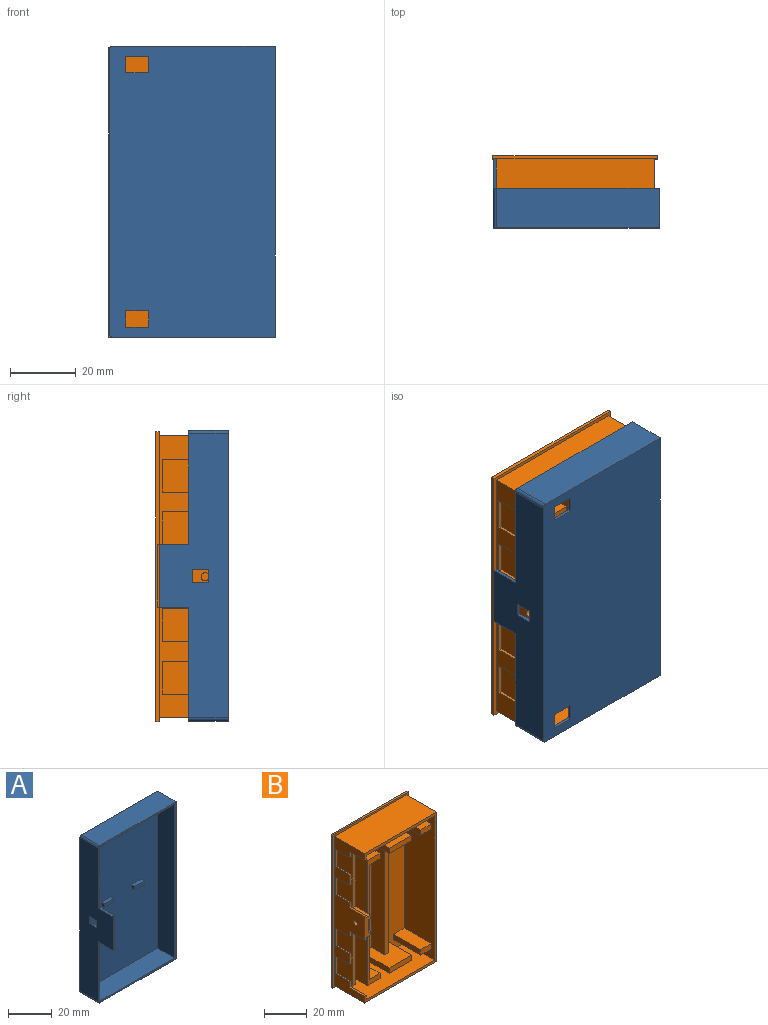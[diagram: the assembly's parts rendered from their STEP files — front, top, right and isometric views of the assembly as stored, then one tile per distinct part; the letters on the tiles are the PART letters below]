
ASSEMBLY  parts=2 mates=1
PART A: 38 faces, bbox 50.5x21.5x88.5 mm
  f0: plane 86.5x21.5mm, normal (-1,0,0), area 1198.5mm2, adj f2,f3,f16,f20,f21,f22,f23,f34
  f1: plane 86.5x20.5mm, normal (1,0,0), area 1112mm2, adj f15,f17,f19,f20,f21,f22,f23,f34
  f2: cylinder r=1mm len=12mm, axis (0,1,0), area 18.8mm2, adj f0,f14,f16,f20
  f3: cylinder r=1mm len=12mm, axis (0,1,0), area 18.8mm2, adj f0,f4,f16,f20
  f4: plane 49.5x12mm, normal (0,0,-1), area 594mm2, adj f3,f5,f16,f20
  f5: plane 88.5x12mm, normal (1,0,0), area 1062mm2, adj f4,f14,f16,f20
  f6: plane 5x1mm, normal (1,0,0), area 5mm2, adj f7,f12,f15,f16
  f7: plane 7x1mm, normal (0,0,-1), area 7mm2, adj f6,f8,f15,f16
  f8: plane 5x1mm, normal (-1,0,0), area 5mm2, adj f7,f12,f15,f16
  f9: plane 7x1mm, normal (0,0,1), area 7mm2, adj f10,f13,f15,f16
  f10: plane 5x1mm, normal (1,0,0), area 5mm2, adj f9,f11,f15,f16
  f11: plane 7x1mm, normal (0,0,-1), area 7mm2, adj f10,f13,f15,f16
  f12: plane 7x1mm, normal (0,0,1), area 7mm2, adj f6,f8,f15,f16
  f13: plane 5x1mm, normal (-1,0,0), area 5mm2, adj f9,f11,f15,f16
  f14: plane 49.5x12mm, normal (0,0,1), area 594mm2, adj f2,f5,f16,f20
  f15: plane 86.5x48.5mm, normal (0,-1,0), area 4101.2mm2, adj f1,f6,f7,f8,f9,f10,f11,f12
  f16: plane 88.5x50.5mm, normal (0,1,0), area 4398.8mm2, adj f0,f2,f3,f4,f5,f6,f7,f8
  f17: plane 48.5x11mm, normal (0,0,-1), area 533.5mm2, adj f1,f15,f18,f20
  f18: plane 86.5x11mm, normal (-1,0,0), area 951.5mm2, adj f15,f17,f19,f20
  f19: plane 48.5x11mm, normal (0,0,1), area 533.5mm2, adj f1,f15,f18,f20
  f20: plane 88.5x50.5mm, normal (0,-1,0), area 254.6mm2, adj f0,f1,f2,f3,f4,f5,f14,f17
  f21: plane 9.5x1mm, normal (0,0,1), area 9.5mm2, adj f0,f1,f20,f23
  f22: plane 9.5x1mm, normal (0,0,-1), area 9.5mm2, adj f0,f1,f20,f23
  f23: plane 19x1mm, normal (0,-1,0), area 19mm2, adj f0,f1,f21,f22
  f24: plane 6x2mm, normal (0,0,1), area 12mm2, adj f15,f25,f27,f28
  f25: plane 2x2mm, normal (-1,0,0), area 4mm2, adj f15,f24,f26,f28
  f26: plane 6x2mm, normal (0,0,-1), area 12mm2, adj f15,f25,f27,f28
  f27: plane 2x2mm, normal (1,0,0), area 4mm2, adj f15,f24,f26,f28
  f28: plane 6x2mm, normal (0,-1,0), area 12mm2, adj f24,f25,f26,f27
  f29: plane 6x2mm, normal (0,0,1), area 12mm2, adj f15,f30,f32,f33
  f30: plane 2x2mm, normal (-1,0,0), area 4mm2, adj f15,f29,f31,f33
  f31: plane 6x2mm, normal (0,0,-1), area 12mm2, adj f15,f30,f32,f33
  f32: plane 2x2mm, normal (1,0,0), area 4mm2, adj f15,f29,f31,f33
  f33: plane 6x2mm, normal (0,-1,0), area 12mm2, adj f29,f30,f31,f32
  f34: plane 5x1mm, normal (0,0,-1), area 5mm2, adj f0,f1,f35,f37
  f35: plane 4x1mm, normal (0,-1,0), area 4mm2, adj f0,f1,f34,f36
  f36: plane 5x1mm, normal (0,0,1), area 5mm2, adj f0,f1,f35,f37
  f37: plane 4x1mm, normal (0,1,0), area 4mm2, adj f0,f1,f34,f36
PART B: 103 faces, bbox 50.2x21x88.2 mm
  f0: plane 88.2x50.2mm, normal (0,-1,0), area 299.6mm2, adj f11,f12,f13,f14,f22,f23,f24,f25
  f1: plane 15x1mm, normal (0,-1,0), area 15mm2, adj f57,f94,f95,f96
  f2: plane 83x45.5mm, normal (0,-1,0), area 3113.8mm2, adj f8,f9,f10,f17,f18,f19,f20,f27
  f3: plane 15x1mm, normal (0,-1,0), area 15mm2, adj f61,f98,f99,f100
  f4: plane 15x1mm, normal (0,-1,0), area 15mm2, adj f59,f82,f83,f84
  f5: plane 7.5x7mm, normal (-1,0,0), area 52.5mm2, adj f35,f65,f67,f75
  f6: plane 30.25x8mm, normal (-1,0,0), area 242mm2, adj f27,f35,f68,f88
  f7: plane 15x1mm, normal (0,-1,0), area 15mm2, adj f55,f85,f86,f87
  f8: plane 18x14.91mm, normal (0,0,-1), area 244.1mm2, adj f2,f45,f46,f47,f52,f53,f54
  f9: plane 18x14.91mm, normal (0,0,1), area 244.1mm2, adj f2,f49,f50,f51,f52,f53,f54
  f10: plane 83x20mm, normal (-1,0,0), area 1552mm2, adj f2,f18,f19,f26,f36,f38,f39,f40
  f11: plane 50.2x1mm, normal (0,0,1), area 50.2mm2, adj f0,f12,f14,f15
  f12: plane 88.2x1mm, normal (-1,0,0), area 88.2mm2, adj f0,f11,f13,f15
  f13: plane 50.2x1mm, normal (0,0,-1), area 50.2mm2, adj f0,f12,f14,f15
  f14: plane 88.2x1mm, normal (1,0,0), area 88.2mm2, adj f0,f11,f13,f15
  f15: plane 88.2x50.2mm, normal (0,1,0), area 4427.6mm2, adj f11,f12,f13,f14
  f16: plane 10x1mm, normal (0,0,-1), area 10mm2, adj f17,f22,f26,f88
  f17: plane 20x2.25mm, normal (1,0,0), area 45mm2, adj f2,f16,f18,f26,f81
  f18: plane 45.5x20mm, normal (0,0,-1), area 910mm2, adj f2,f10,f17,f26
  f19: plane 45.5x20mm, normal (0,0,1), area 910mm2, adj f2,f10,f20,f26
  f20: plane 20x2.25mm, normal (1,0,0), area 45mm2, adj f2,f19,f21,f26,f97
  f21: plane 10x1mm, normal (0,0,1), area 10mm2, adj f20,f22,f26,f101
  f22: plane 86x20mm, normal (-1,0,0), area 705.1mm2, adj f0,f16,f21,f23,f25,f26,f56,f58
  f23: plane 48x20mm, normal (0,0,-1), area 960mm2, adj f0,f22,f24,f26
  f24: plane 86x20mm, normal (1,0,0), area 1720mm2, adj f0,f23,f25,f26
  f25: plane 48x20mm, normal (0,0,1), area 960mm2, adj f0,f22,f24,f26
  f26: plane 86x48mm, normal (0,-1,0), area 273mm2, adj f10,f16,f17,f18,f19,f20,f21,f22
  f27: plane 18x8.29mm, normal (0,0,1), area 149.3mm2, adj f2,f6,f34,f35,f80
  f28: plane 30.25x8mm, normal (-1,0,0), area 242mm2, adj f29,f35,f73,f101
  f29: plane 18x8.29mm, normal (0,0,-1), area 149.3mm2, adj f2,f28,f30,f35,f92
  f30: plane 18x3mm, normal (1,0,0), area 54mm2, adj f2,f29,f31,f35
  f31: plane 18x7.29mm, normal (0,0,1), area 131.3mm2, adj f2,f30,f32,f35
  f32: plane 66x18mm, normal (1,0,0), area 1188mm2, adj f2,f31,f33,f35
  f33: plane 18x7.29mm, normal (0,0,-1), area 131.3mm2, adj f2,f32,f34,f35
  f34: plane 18x3mm, normal (1,0,0), area 54mm2, adj f2,f27,f33,f35
  f35: plane 72x8.29mm, normal (0,-1,0), area 115.8mm2, adj f5,f6,f27,f28,f29,f30,f31,f32
  f36: plane 18x7.29mm, normal (0,0,1), area 131.3mm2, adj f2,f10,f37,f39
  f37: plane 18x3mm, normal (-1,0,0), area 54mm2, adj f2,f36,f38,f39
  f38: plane 18x7.29mm, normal (0,0,-1), area 131.3mm2, adj f2,f10,f37,f39
  f39: plane 7.29x3mm, normal (0,-1,0), area 21.9mm2, adj f10,f36,f37,f38
  f40: plane 18x7.29mm, normal (0,0,1), area 131.3mm2, adj f2,f10,f41,f43
  f41: plane 18x3mm, normal (-1,0,0), area 54mm2, adj f2,f40,f42,f43
  f42: plane 18x7.29mm, normal (0,0,-1), area 131.3mm2, adj f2,f10,f41,f43
  f43: plane 7.29x3mm, normal (0,-1,0), area 21.9mm2, adj f10,f40,f41,f42
  f44: plane 18x14.91mm, normal (0,0,1), area 268.4mm2, adj f2,f45,f46,f47
  f45: plane 18x3mm, normal (-1,0,0), area 54mm2, adj f2,f8,f44,f47
  f46: plane 18x3mm, normal (1,0,0), area 54mm2, adj f2,f8,f44,f47
  f47: plane 14.91x3mm, normal (0,-1,0), area 44.7mm2, adj f8,f44,f45,f46
  f48: plane 18x14.91mm, normal (0,0,-1), area 268.4mm2, adj f2,f49,f50,f51
  f49: plane 18x3mm, normal (1,0,0), area 54mm2, adj f2,f9,f48,f51
  f50: plane 18x3mm, normal (-1,0,0), area 54mm2, adj f2,f9,f48,f51
  f51: plane 14.91x3mm, normal (0,-1,0), area 44.7mm2, adj f9,f48,f49,f50
  f52: plane 66x9mm, normal (-1,0,0), area 594mm2, adj f2,f8,f9,f54
  f53: plane 66x9mm, normal (1,0,0), area 594mm2, adj f2,f8,f9,f54
  f54: plane 66x2.7mm, normal (0,-1,0), area 178.2mm2, adj f8,f9,f52,f53
  f55: plane 15x10mm, normal (1,0,0), area 60mm2, adj f7,f56,f76,f79,f85,f87,f88
  f56: plane 10x1mm, normal (0,-1,0), area 10mm2, adj f22,f55,f76,f79
  f57: plane 15x10mm, normal (1,0,0), area 60mm2, adj f1,f58,f90,f91,f94,f96,f101
  f58: plane 10x1mm, normal (0,-1,0), area 10mm2, adj f22,f57,f90,f91
  f59: plane 15x10mm, normal (1,0,0), area 60mm2, adj f4,f60,f77,f78,f82,f84,f88
  f60: plane 10x1mm, normal (0,-1,0), area 10mm2, adj f22,f59,f77,f78
  f61: plane 15x10mm, normal (1,0,0), area 60mm2, adj f3,f62,f89,f93,f98,f100,f101
  f62: plane 10x1mm, normal (0,-1,0), area 10mm2, adj f22,f61,f89,f93
  f63: plane 2x2mm, normal (1,0,0), area 4mm2, adj f35,f65,f73,f74
  f64: plane 2x2mm, normal (1,0,0), area 4mm2, adj f35,f67,f68,f74
  f65: plane 9x1.5mm, normal (0,0,1), area 13.5mm2, adj f5,f63,f66,f74,f75
  f66: plane 9x7.5mm, normal (1,0,0), area 62.6mm2, adj f65,f67,f74,f75,f102
  f67: plane 9x1.5mm, normal (0,0,-1), area 13.5mm2, adj f5,f64,f66,f74,f75
  f68: plane 10x3mm, normal (0,0,1), area 30mm2, adj f6,f64,f69,f74,f88
  f69: plane 10x1mm, normal (1,0,0), area 10mm2, adj f68,f70,f74,f88
  f70: plane 10x1mm, normal (0,0,1), area 10mm2, adj f22,f69,f74,f88
  f71: plane 10x1mm, normal (0,0,-1), area 10mm2, adj f22,f72,f74,f101
  f72: plane 10x1mm, normal (1,0,0), area 10mm2, adj f71,f73,f74,f101
  f73: plane 10x3mm, normal (0,0,-1), area 30mm2, adj f28,f63,f72,f74,f101
  f74: plane 13.5x4mm, normal (0,-1,0), area 36.8mm2, adj f22,f63,f64,f65,f66,f67,f68,f69
  f75: plane 7.5x1.5mm, normal (0,-1,0), area 11.2mm2, adj f5,f65,f66,f67
  f76: plane 9x1mm, normal (0,0,1), area 9mm2, adj f22,f55,f56,f88
  f77: plane 9x1mm, normal (0,0,-1), area 9mm2, adj f22,f59,f60,f88
  f78: plane 9x1mm, normal (0,0,1), area 9mm2, adj f22,f59,f60,f88
  f79: plane 9x1mm, normal (0,0,-1), area 9mm2, adj f22,f55,f56,f88
  f80: plane 10x3.25mm, normal (1,0,0), area 32.5mm2, adj f2,f27,f81,f88
  f81: plane 10x3mm, normal (0,0,1), area 30mm2, adj f2,f17,f80,f88
  f82: plane 10x1mm, normal (0,0,-1), area 10mm2, adj f4,f59,f83,f88
  f83: plane 15x10mm, normal (-1,0,0), area 150mm2, adj f4,f82,f84,f88
  f84: plane 10x1mm, normal (0,0,1), area 10mm2, adj f4,f59,f83,f88
  f85: plane 10x1mm, normal (0,0,-1), area 10mm2, adj f7,f55,f86,f88
  f86: plane 15x10mm, normal (-1,0,0), area 150mm2, adj f7,f85,f87,f88
  f87: plane 10x1mm, normal (0,0,1), area 10mm2, adj f7,f55,f86,f88
  f88: plane 33.5x4mm, normal (0,-1,0), area 83mm2, adj f6,f16,f22,f55,f59,f68,f69,f70
  f89: plane 9x1mm, normal (0,0,1), area 9mm2, adj f22,f61,f62,f101
  f90: plane 9x1mm, normal (0,0,-1), area 9mm2, adj f22,f57,f58,f101
  f91: plane 9x1mm, normal (0,0,1), area 9mm2, adj f22,f57,f58,f101
  f92: plane 10x3.25mm, normal (1,0,0), area 32.5mm2, adj f2,f29,f97,f101
  f93: plane 9x1mm, normal (0,0,-1), area 9mm2, adj f22,f61,f62,f101
  f94: plane 10x1mm, normal (0,0,-1), area 10mm2, adj f1,f57,f95,f101
  f95: plane 15x10mm, normal (-1,0,0), area 150mm2, adj f1,f94,f96,f101
  f96: plane 10x1mm, normal (0,0,1), area 10mm2, adj f1,f57,f95,f101
  f97: plane 10x3mm, normal (0,0,-1), area 30mm2, adj f2,f20,f92,f101
  f98: plane 10x1mm, normal (0,0,-1), area 10mm2, adj f3,f61,f99,f101
  f99: plane 15x10mm, normal (-1,0,0), area 150mm2, adj f3,f98,f100,f101
  f100: plane 10x1mm, normal (0,0,1), area 10mm2, adj f3,f61,f99,f101
  f101: plane 33.5x4mm, normal (0,-1,0), area 83mm2, adj f21,f22,f28,f57,f61,f71,f72,f73
  f102: cylinder r=1.25mm len=2.5mm, axis (-1,0,0), area 19.6mm2, adj f22,f66
PLACE A rot(axis=(1,0,0),180deg) t=(-47.5,-23,81.82)mm
PLACE B t=(0,-1,-0.2)mm
MATE fastened A.f2 <-> B.f26  axis (0,1,0) through (-46.5,-22,-5.68)mm
